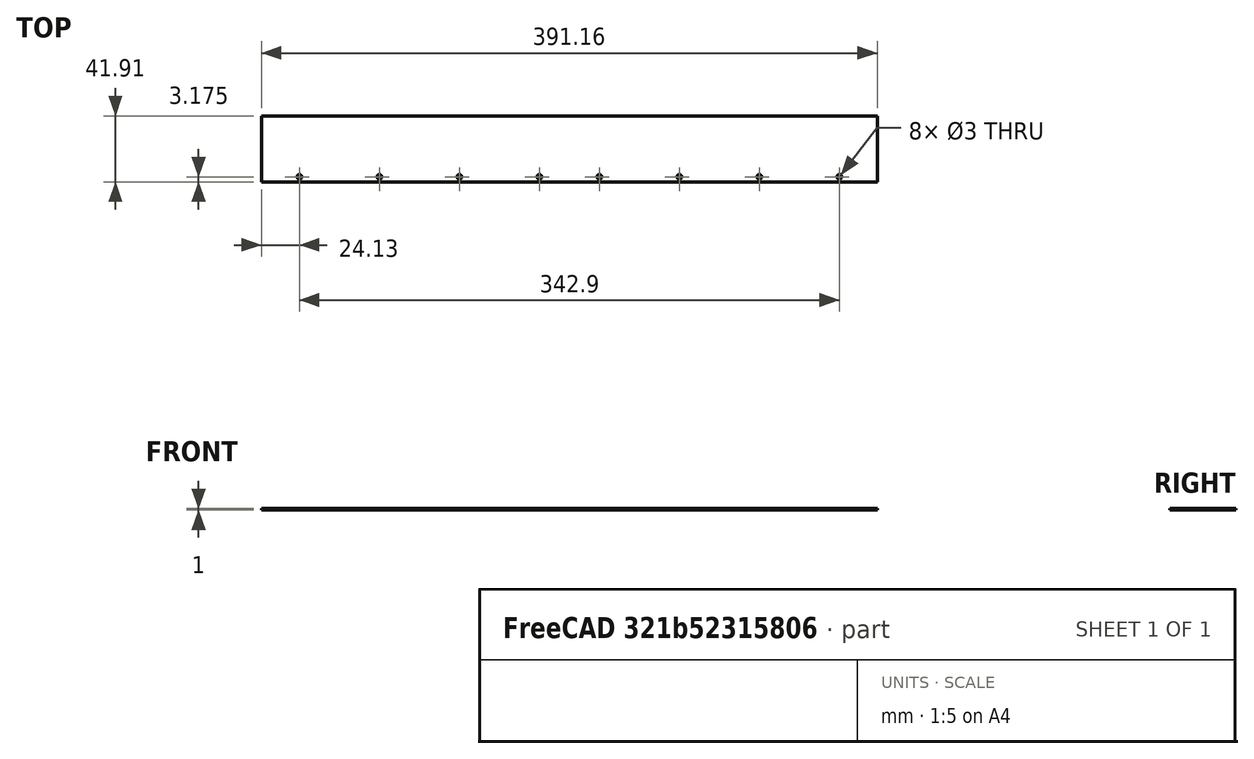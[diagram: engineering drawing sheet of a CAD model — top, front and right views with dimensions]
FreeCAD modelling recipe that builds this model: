
FCSTD DOCUMENT  (FreeCAD 1.0R38641 +468 (Git))
Label: doepfer_bus_board_v6
License: All rights reserved
LicenseURL: https://en.wikipedia.org/wiki/All_rights_reserved
objects: Sketcher::SketchObject×1, PartDesign::Pad×1, PartDesign::Body×1
note: 6 computed .brp shape members not serialized (recipe doc carries the construction recipe); baked Part::Feature solids carry a one-line shape summary decoded from their .brp

FEATURE [Sketcher::SketchObject] Sketch
  ArcFitTolerance = 1e-06
  AttachmentSupport = -> [XY_Plane]
  FullyConstrained = true
  MakeInternals = false
  MapMode = 5
  sketch-geometry (19):
    g0: LineSegment StartX=0 StartY=41.91 StartZ=0 EndX=0 EndY=0 EndZ=0
    g1: LineSegment StartX=0 StartY=0 StartZ=0 EndX=391.16 EndY=0 EndZ=0
    g2: LineSegment StartX=391.16 StartY=0 StartZ=0 EndX=391.16 EndY=41.91 EndZ=0
    g3: LineSegment StartX=391.16 StartY=41.91 StartZ=0 EndX=0 EndY=41.91 EndZ=0
    g4: Circle CenterX=24.13 CenterY=3.175 CenterZ=0 NormalX=0 NormalY=0 NormalZ=1 AngleXU=0 Radius=1.5
    g5: Circle [constr] CenterX=49.53 CenterY=3.175 CenterZ=0 NormalX=0 NormalY=0 NormalZ=1 AngleXU=0 Radius=1.5
    g6: Circle CenterX=74.93 CenterY=3.175 CenterZ=0 NormalX=0 NormalY=0 NormalZ=1 AngleXU=0 Radius=1.5
    g7: Circle [constr] CenterX=100.33 CenterY=3.175 CenterZ=0 NormalX=0 NormalY=0 NormalZ=1 AngleXU=0 Radius=1.5
    g8: Circle CenterX=125.73 CenterY=3.175 CenterZ=0 NormalX=0 NormalY=0 NormalZ=1 AngleXU=0 Radius=1.5
    g9: Circle CenterX=176.53 CenterY=3.175 CenterZ=0 NormalX=0 NormalY=0 NormalZ=1 AngleXU=0 Radius=1.5
    g10: Circle [constr] CenterX=151.13 CenterY=3.175 CenterZ=0 NormalX=0 NormalY=0 NormalZ=1 AngleXU=0 Radius=1.5
    g11: LineSegment [constr] StartX=0 StartY=3.175 StartZ=0 EndX=391.16 EndY=3.175 EndZ=0
    g12: Circle CenterX=214.63 CenterY=3.175 CenterZ=0 NormalX=0 NormalY=0 NormalZ=1 AngleXU=0 Radius=1.5
    g13: Circle [constr] CenterX=240.03 CenterY=3.175 CenterZ=0 NormalX=0 NormalY=0 NormalZ=1 AngleXU=0 Radius=1.5
    g14: Circle CenterX=265.43 CenterY=3.175 CenterZ=0 NormalX=0 NormalY=0 NormalZ=1 AngleXU=0 Radius=1.5
    g15: Circle [constr] CenterX=290.83 CenterY=3.175 CenterZ=0 NormalX=0 NormalY=0 NormalZ=1 AngleXU=0 Radius=1.5
    g16: Circle CenterX=316.23 CenterY=3.175 CenterZ=0 NormalX=0 NormalY=0 NormalZ=1 AngleXU=0 Radius=1.5
    g17: Circle [constr] CenterX=341.63 CenterY=3.175 CenterZ=0 NormalX=0 NormalY=0 NormalZ=1 AngleXU=0 Radius=1.5
    g18: Circle CenterX=367.03 CenterY=3.175 CenterZ=0 NormalX=0 NormalY=0 NormalZ=1 AngleXU=0 Radius=1.5
  constraints (52):
    c: Coincident(g0,g1)
    c: Coincident(g1,g2)
    c: Coincident(g2,g3)
    c: Coincident(g3,g0)
    c: Vertical(g0)
    c: Vertical(g2)
    c: Horizontal(g1)
    c: Horizontal(g3)
    c: Coincident(g0,g-1)
    c: DistanceX(g1,g1) = 391.16
    c: DistanceY(g0,g0) = 41.91
    c: PointOnObject(g11,g0)
    c: PointOnObject(g11,g2)
    c: Horizontal(g11)
    c: DistanceY(g0,g11) = 3.175
    c: PointOnObject(g4,g11)
    c: PointOnObject(g5,g11)
    c: PointOnObject(g6,g11)
    c: PointOnObject(g7,g11)
    c: PointOnObject(g8,g11)
    c: PointOnObject(g9,g11)
    c: PointOnObject(g10,g11)
    c: DistanceX(g11,g4) = 24.13
    c: DistanceX(g4,g5) = 25.4
    c: DistanceX(g5,g6) = 25.4
    c: DistanceX(g6,g7) = 25.4
    c: Distance(g7,g8) = 25.4
    c: Distance(g8,g10) = 25.4
    c: DistanceX(g10,g9) = 25.4
    c: PointOnObject(g12,g11)
    c: PointOnObject(g13,g11)
    c: PointOnObject(g14,g11)
    c: PointOnObject(g15,g11)
    c: PointOnObject(g16,g11)
    c: PointOnObject(g17,g11)
    c: PointOnObject(g18,g11)
    c: DistanceX(g9,g12) = 38.1
    c: DistanceX(g12,g13) = 25.4
    c: DistanceX(g13,g14) = 25.4
    c: DistanceX(g14,g15) = 25.4
    c: DistanceX(g15,g16) = 25.4
    c: DistanceX(g16,g17) = 25.4
    c: DistanceX(g17,g18) = 25.4
    c: Diameter(g4) = 3  'HoleDiameter'
    c: Equal(g4, g5-g8) x4
    c: Equal(g4,g10)
    c: Equal(g4,g9)
    c: Equal(g4, g12-g15) x4
    c: Equal(g16,g4)
    c: Equal(g4,g17)
    c: Equal(g18,g4)
    c: DistanceX(g18,g11) = 24.13
FEATURE [PartDesign::Pad] Pad
  Direction = (0,0,1)
  Length = 1
  Length2 = 10
  Profile = -> Sketch
  ReferenceAxis = -> Sketch [N_Axis]
  Refine = true
  Suppressed = false
  Type = 0
FEATURE [PartDesign::Body] Body  label="BusBoard"
  AllowCompound = false
  Group = -> [Sketch,Pad]
  Origin = -> Origin
  Tip = -> Pad
